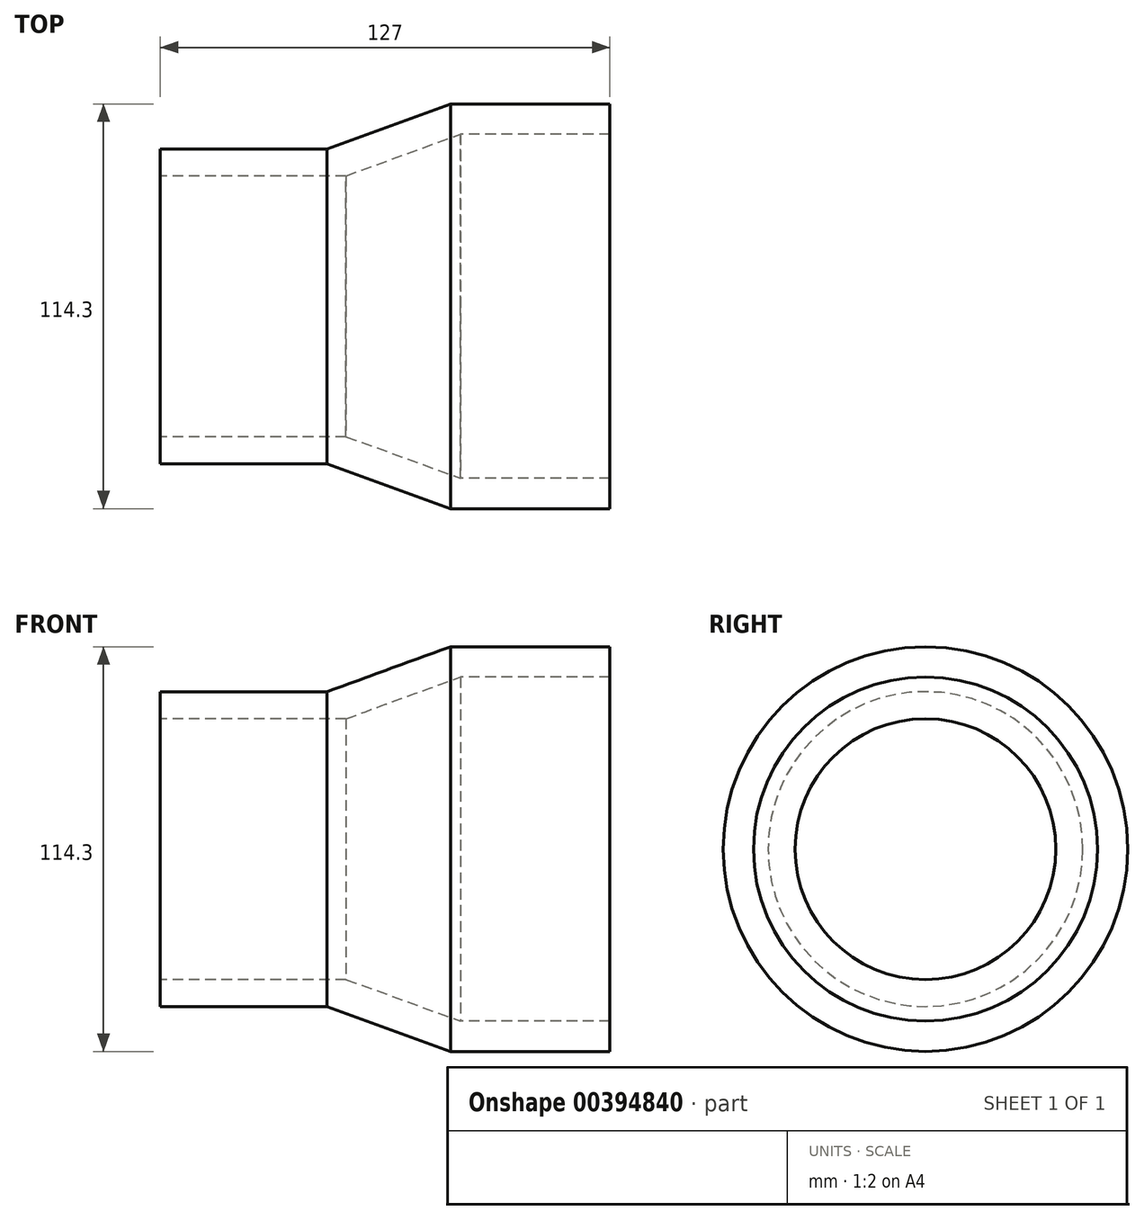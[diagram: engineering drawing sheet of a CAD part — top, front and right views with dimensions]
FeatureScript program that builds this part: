
annotation { "Feature Type Name" : "Feature", "Feature Type Description" : "" }
export const myFeature = defineFeature(function(context is Context, id is Id, definition is map)
    precondition{}
    {
        {
            var Q0;
            Q0=qCreatedBy(makeId("Front.planeOp"),FACE);
            var sketch = newSketch(context, id + "F0", { "sketchPlane" : qUnion([Q0])});
            skLineSegment(sketch, "E0", {"start": v(0, 0) * mm, "end": v(127, 0) * mm});
            skLineSegment(sketch, "E1", {"start": v(127, 48.6) * mm, "end": v(127, 57.15) * mm});
            skLineSegment(sketch, "E2", {"start": v(127, 48.6) * mm, "end": v(84.8, 48.6) * mm});
            skLineSegment(sketch, "E3", {"start": v(84.8, 48.6) * mm, "end": v(52.49, 36.83) * mm});
            skLineSegment(sketch, "E4", {"start": v(52.49, 36.83) * mm, "end": v(0, 36.83) * mm});
            skLineSegment(sketch, "E5", {"start": v(0, 44.45) * mm, "end": v(0, 36.83) * mm});
            skLineSegment(sketch, "E6.0", {"start": v(47.1, 44.45) * mm, "end": v(0, 44.45) * mm});
            skLineSegment(sketch, "E7.0", {"start": v(127, 57.15) * mm, "end": v(82, 57.15) * mm});
            skLineSegment(sketch, "E8.0", {"start": v(82, 57.15) * mm, "end": v(47.1, 44.45) * mm});
            skSolve(sketch);
        }
        {
            var Q0;
            Q0=makeQuery(id+"F0.imprint","IMPRINT",FACE,{"disambiguationData":[TD([[makeQuery(id+"F0.imprint","IMPRINT",EDGE,{"derivedFrom":sQuery(id+"F0.wireOp",EDGE,"E1")}),1.0]])]});
            var Q1;
            Q1=sQuery(id+"F0.wireOp",EDGE,"E0");
            revolve(context, id + "F1", {"entities" : qUnion([Q0]), "axis" : qUnion([Q1]), "revolveType" : RevolveType.FULL});
        }
    });
